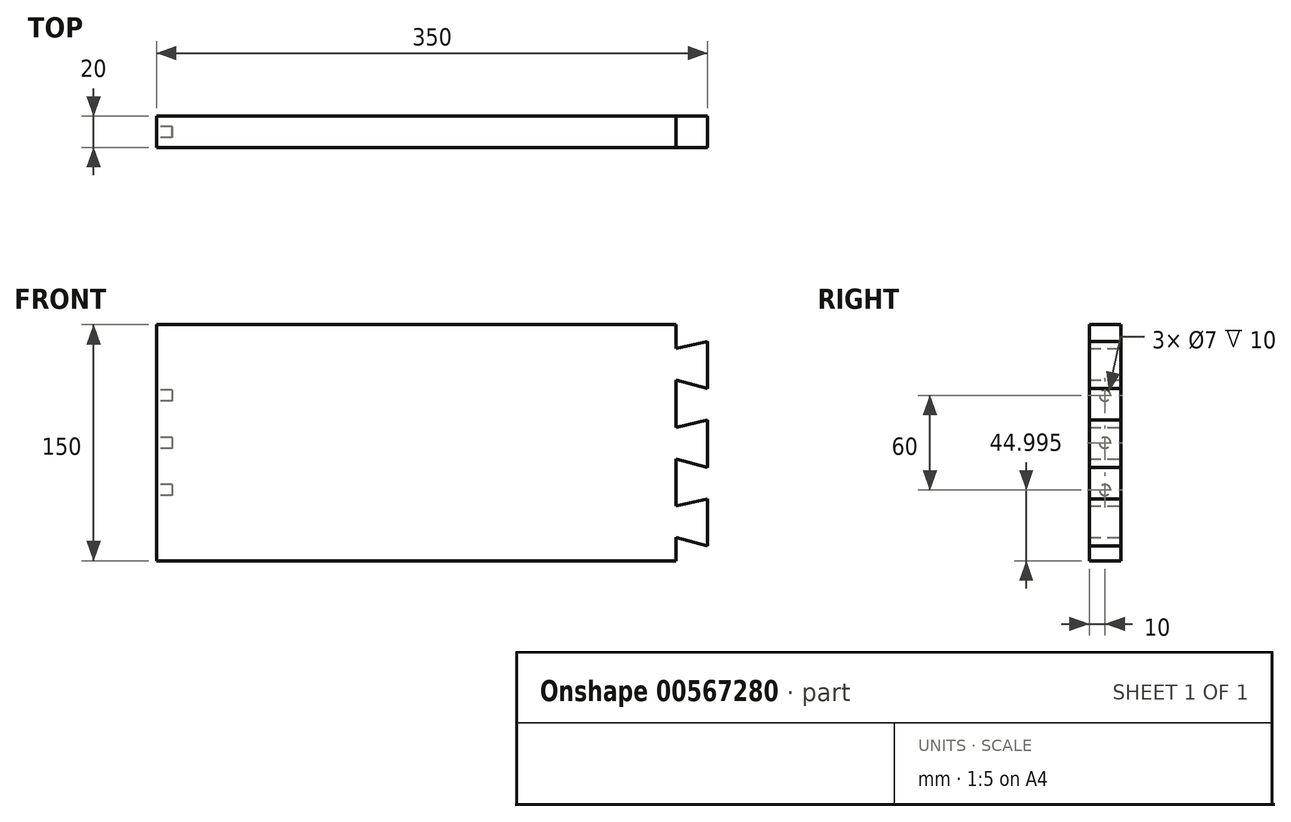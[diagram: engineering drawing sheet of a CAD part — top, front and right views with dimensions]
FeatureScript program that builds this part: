
annotation { "Feature Type Name" : "Feature", "Feature Type Description" : "" }
export const myFeature = defineFeature(function(context is Context, id is Id, definition is map)
    precondition{}
    {
        {
            var Q0;
            Q0=qCreatedBy(makeId("Front.planeOp"),FACE);
            var sketch = newSketch(context, id + "F0", { "sketchPlane" : qUnion([Q0])});
            skLineSegment(sketch, "E0.bottom", {"start": v(159.38, -61.85) * mm, "end": v(-170.62, -61.85) * mm});
            skLineSegment(sketch, "E0.top", {"start": v(159.38, 88.15) * mm, "end": v(-170.62, 88.15) * mm});
            skLineSegment(sketch, "E0.left", {"start": v(179.38, -52.51) * mm, "end": v(179.38, -22.51) * mm});
            skLineSegment(sketch, "E0.right", {"start": v(-170.62, -61.85) * mm, "end": v(-170.62, 88.15) * mm});
            skLineSegment(sketch, "E1", {"start": v(159.38, 88.15) * mm, "end": v(159.38, 72.94) * mm});
            skLineSegment(sketch, "E2", {"start": v(179.38, 13.15) * mm, "end": v(179.38, 27.49) * mm});
            skLineSegment(sketch, "E3", {"start": v(179.38, 13.15) * mm, "end": v(179.38, -2.51) * mm});
            skLineSegment(sketch, "E4", {"start": v(179.38, 27.49) * mm, "end": v(159.38, 22.94) * mm});
            skLineSegment(sketch, "E5", {"start": v(159.38, 2.94) * mm, "end": v(179.38, -2.51) * mm});
            skLineSegment(sketch, "E6", {"start": v(159.38, 2.94) * mm, "end": v(159.38, -27.06) * mm});
            skLineSegment(sketch, "E7", {"start": v(159.38, 22.94) * mm, "end": v(159.38, 52.94) * mm});
            skLineSegment(sketch, "E8", {"start": v(179.38, 47.49) * mm, "end": v(159.38, 52.94) * mm});
            skLineSegment(sketch, "E9", {"start": v(159.38, -27.06) * mm, "end": v(179.38, -22.51) * mm});
            skLineSegment(sketch, "E10", {"start": v(179.38, 47.49) * mm, "end": v(179.38, 77.49) * mm});
            skLineSegment(sketch, "E11", {"start": v(179.38, -22.51) * mm, "end": v(179.38, -52.51) * mm});
            skLineSegment(sketch, "E12", {"start": v(179.38, -52.51) * mm, "end": v(159.38, -47.06) * mm});
            skLineSegment(sketch, "E13", {"start": v(159.38, 72.94) * mm, "end": v(179.38, 77.49) * mm});
            skPoint(sketch, "E14.orphan", {"position": v(179.38, 88.15) * mm});
            skLineSegment(sketch, "E15.trimOffspring", {"start": v(179.38, -2.51) * mm, "end": v(179.38, 27.49) * mm});
            skPoint(sketch, "E16.orphan", {"position": v(179.38, -61.85) * mm});
            skPoint(sketch, "E17.start.orphan", {"position": v(159.38, 13.15) * mm});
            skLineSegment(sketch, "E18.trimOffspring", {"start": v(159.38, 52.94) * mm, "end": v(159.38, 22.94) * mm});
            skLineSegment(sketch, "E19.trimOffspring", {"start": v(159.38, -47.06) * mm, "end": v(159.38, -61.85) * mm});
            skSolve(sketch);
        }
        {
            var Q0;
            Q0 = qSketchRegion(id + "F0", true);
            extrude(context, id + "F1", {"entities" : qUnion([Q0]), "depth" : 20 * mm, "offsetDistance" : 25 * mm});
        }
        {
            var Q0;
            Q0=makeQuery(id+"F1.opExtrude","SWEPT_FACE",FACE,{"disambiguationData":[OSD([sQuery(id+"F0.wireOp",EDGE,"E0.right")])]});
            var sketch = newSketch(context, id + "F2", { "sketchPlane" : qUnion([Q0])});
            skCircle(sketch, "E20", {"center": v(10, 13.15) * mm, "radius": 3.5 * mm});
            skPoint(sketch, "E20.centerSnap0", {"position": v(0, 13.15) * mm});
            skPoint(sketch, "E20.centerSnap1", {"position": v(10, -61.85) * mm});
            skCircle(sketch, "E21", {"center": v(10, 43.15) * mm, "radius": 3.5 * mm});
            skCircle(sketch, "E22", {"center": v(10, -16.85) * mm, "radius": 3.5 * mm});
            skSolve(sketch);
        }
        {
            var Q0;
            Q0 = qSketchRegion(id + "F2", true);
            extrude(context, id + "F3", {"entities" : qUnion([Q0]), "operationType" : NewBodyOperationType.REMOVE, "oppositeDirection" : true, "depth" : 10 * mm, "offsetDistance" : 25 * mm});
        }
    });
